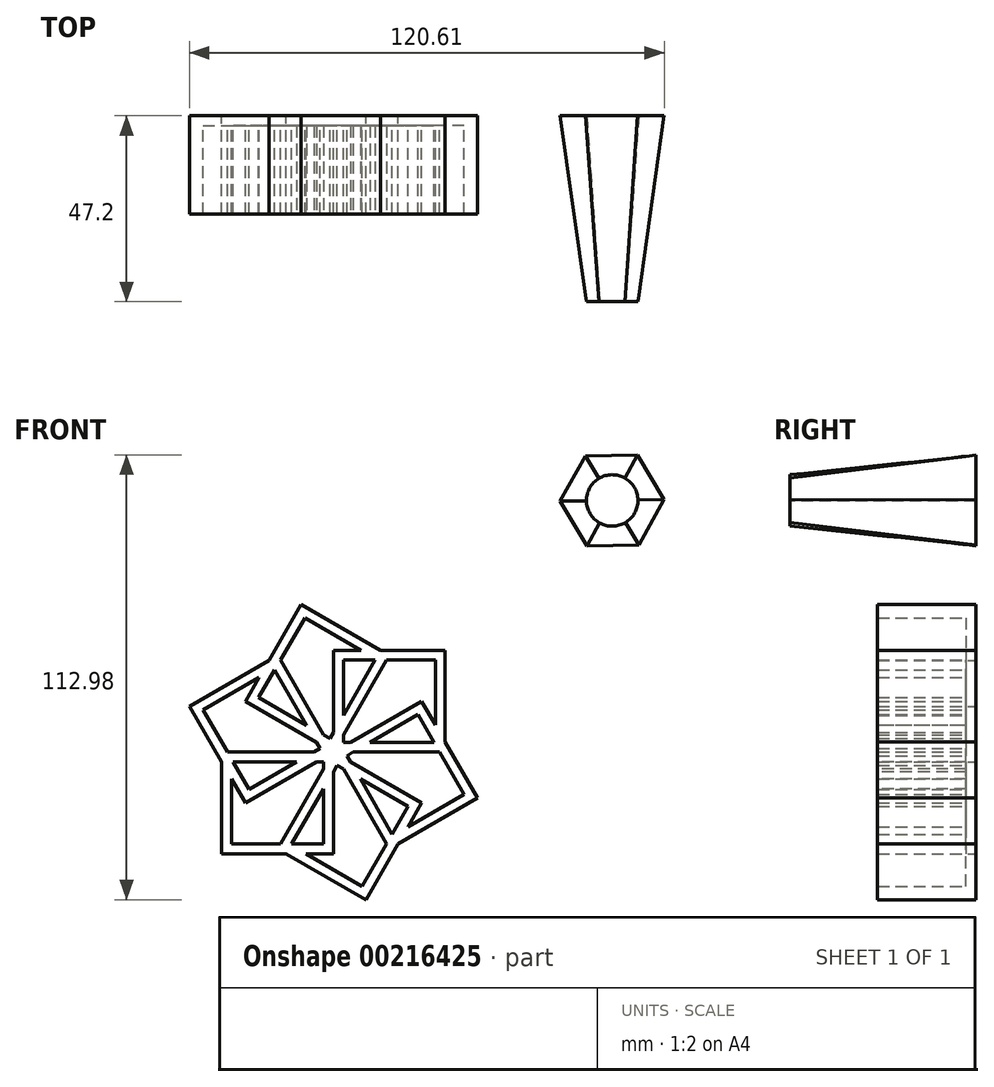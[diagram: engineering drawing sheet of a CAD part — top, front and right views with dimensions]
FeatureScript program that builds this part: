
annotation { "Feature Type Name" : "Feature", "Feature Type Description" : "" }
export const myFeature = defineFeature(function(context is Context, id is Id, definition is map)
    precondition{}
    {
        {
            var Q0;
            Q0=qCreatedBy(makeId("Front.planeOp"),FACE);
            var sketch = newSketch(context, id + "F0", { "sketchPlane" : qUnion([Q0])});
            skLineSegment(sketch, "E0.bottom", {"start": v(0, 0) * mm, "end": v(-28.39, 0) * mm});
            skLineSegment(sketch, "E0.top", {"start": v(0, -25.86) * mm, "end": v(-28.39, -25.86) * mm});
            skLineSegment(sketch, "E0.left", {"start": v(0, 0) * mm, "end": v(0, -25.86) * mm});
            skLineSegment(sketch, "E0.right", {"start": v(-28.39, 0) * mm, "end": v(-28.39, -25.86) * mm});
            skCircle(sketch, "E1.cCircle", {"center": v(42.41, 38.07) * mm, "radius": 11.44 * mm, "construction": true});
            skLineSegment(sketch, "E1.0", {"start": v(29.2, 37.89) * mm, "end": v(35.65, 49.42) * mm});
            skLineSegment(sketch, "E1.1", {"start": v(35.65, 49.42) * mm, "end": v(48.86, 49.6) * mm});
            skLineSegment(sketch, "E1.2", {"start": v(48.86, 49.6) * mm, "end": v(55.63, 38.26) * mm});
            skLineSegment(sketch, "E1.3", {"start": v(55.63, 38.26) * mm, "end": v(49.18, 26.73) * mm});
            skLineSegment(sketch, "E1.4", {"start": v(49.18, 26.73) * mm, "end": v(35.97, 26.54) * mm});
            skLineSegment(sketch, "E1.5", {"start": v(35.97, 26.54) * mm, "end": v(29.2, 37.89) * mm});
            skPoint(sketch, "E1.0.midPoint", {"position": v(32.42, 43.65) * mm});
            skSolve(sketch);
        }
        {
            var Q0;
            Q0=makeQuery(id+"F0.imprint","IMPRINT",FACE,{"disambiguationData":[TD([[makeQuery(id+"F0.imprint","IMPRINT",EDGE,{"derivedFrom":sQuery(id+"F0.wireOp",EDGE,"E0.bottom")}),1.0]])]});
            var Q1;
            Q1=makeQuery(id+"F0.imprint","IMPRINT",FACE,{"disambiguationData":[TD([[makeQuery(id+"F0.imprint","IMPRINT",EDGE,{"derivedFrom":sQuery(id+"F0.wireOp",EDGE,"qtQcvDr3-OD6L-YiYm-oJm1-z1p8NA79QfNp.bottom")}),1.0]])]});
            extrude(context, id + "F1", {"entities" : qUnion([Q0, Q1]), "depth" : 25 * mm});
        }
        {
            var Q0;
            Q0=makeQuery(id+"F1.opExtrude","CAP_FACE",FACE,{"disambiguationData":[OSD([sQuery(id+"F0.wireOp",EDGE,"E0.bottom"),sQuery(id+"F0.wireOp",EDGE,"E0.top"),sQuery(id+"F0.wireOp",EDGE,"E0.left"),sQuery(id+"F0.wireOp",EDGE,"E0.right")])],"isStart":false});
            shell(context, id + "F2", {"entities" : qUnion([Q0]), "thickness" : 2.5 * mm});
        }
        {
            var Q0;
            Q0=makeQuery(id+"F1.opExtrude","SWEPT_BODY",BODY,{"disambiguationData":[OSD([sQuery(id+"F0.wireOp",EDGE,"E0.bottom"),sQuery(id+"F0.wireOp",EDGE,"E0.top"),sQuery(id+"F0.wireOp",EDGE,"E0.left"),sQuery(id+"F0.wireOp",EDGE,"E0.right")])]});
            var Q1;
            Q1=makeQuery(id+"F1.opExtrude","SWEPT_EDGE",EDGE,{"disambiguationData":[OSD([sQuery(id+"F0.wireOp",EDGE,"E0.top"),sQuery(id+"F0.wireOp",EDGE,"E0.right")])]});
            circularPattern(context, id + "F3", {"operationType" : NewBodyOperationType.ADD, "entities" : qUnion([Q0]), "axis" : qUnion([Q1]), "angle" : 360 * degree, "instanceCount" : 6, "equalSpace" : true});
        }
        {
            var Q0;
            Q0=makeQuery(id+"F0.imprint","IMPRINT",FACE,{"disambiguationData":[TD([[makeQuery(id+"F0.imprint","IMPRINT",EDGE,{"derivedFrom":sQuery(id+"F0.wireOp",EDGE,"E1.0")}),-1.0]])]});
            cPlane(context, id + "F4", {"entities" : qUnion([Q0]), "cplaneType" : CPlaneType.OFFSET, "offset" : 47.2 * mm, "width" : 150 * mm, "height" : 150 * mm});
        }
        {
            var Q0;
            Q0=qCreatedBy(id+"F4.planeOp",FACE);
            var sketch = newSketch(context, id + "F5", { "sketchPlane" : qUnion([Q0])});
            skPoint(sketch, "E2.0", {"position": v(42.41, 38.07) * mm});
            skCircle(sketch, "E3", {"center": v(42.41, 38.07) * mm, "radius": 6.54 * mm});
            skSolve(sketch);
        }
        {
            var Q0;
            Q0=makeQuery(id+"F0.imprint","IMPRINT",FACE,{"disambiguationData":[TD([[makeQuery(id+"F0.imprint","IMPRINT",EDGE,{"derivedFrom":sQuery(id+"F0.wireOp",EDGE,"E1.0")}),-1.0]])]});
            var Q1;
            Q1=makeQuery(id+"F5.imprint","IMPRINT",FACE,{"disambiguationData":[TD([[makeQuery(id+"F5.imprint","IMPRINT",EDGE,{"derivedFrom":sQuery(id+"F5.wireOp",EDGE,"E3")}),1.0]])]});
            loft(context, id + "F6", {"sheetProfilesArray" : [{ "sheetProfileEntities" : qUnion([Q0]) }, { "sheetProfileEntities" : qUnion([Q1]) }]});
        }
    });
